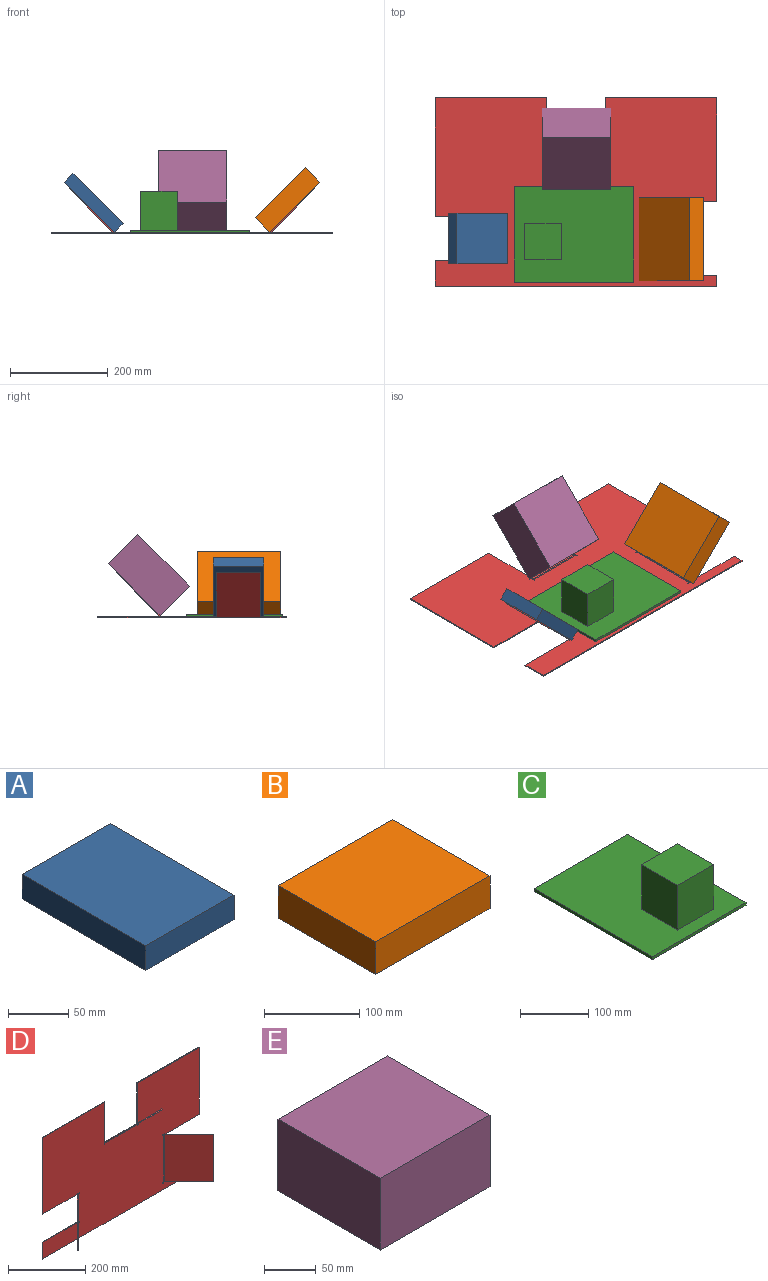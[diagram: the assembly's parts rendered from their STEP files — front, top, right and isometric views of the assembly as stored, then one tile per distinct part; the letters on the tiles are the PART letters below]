
ASSEMBLY  parts=5 mates=4
PART A: 6 faces, bbox 103x145x25 mm
  f0: plane 145x25mm, normal (-1,0,0), area 3625mm2, adj f1,f3,f4,f5
  f1: plane 103x25mm, normal (0,-1,0), area 2575mm2, adj f0,f2,f4,f5
  f2: plane 145x25mm, normal (1,0,0), area 3625mm2, adj f1,f3,f4,f5
  f3: plane 103x25mm, normal (0,1,0), area 2575mm2, adj f0,f2,f4,f5
  f4: plane 145x103mm, normal (0,0,1), area 14935mm2, adj f0,f1,f2,f3
  f5: plane 145x103mm, normal (0,0,-1), area 14935mm2, adj f0,f1,f2,f3
PART B: 6 faces, bbox 170x145x42 mm
  f0: plane 145x42mm, normal (-1,0,0), area 6090mm2, adj f1,f3,f4,f5
  f1: plane 170x42mm, normal (0,-1,0), area 7140mm2, adj f0,f2,f4,f5
  f2: plane 145x42mm, normal (1,0,0), area 6090mm2, adj f1,f3,f4,f5
  f3: plane 170x42mm, normal (0,1,0), area 7140mm2, adj f0,f2,f4,f5
  f4: plane 170x145mm, normal (0,0,1), area 24650mm2, adj f0,f1,f2,f3
  f5: plane 170x145mm, normal (0,0,-1), area 24650mm2, adj f0,f1,f2,f3
PART C: 11 faces, bbox 195x245x85 mm
  f0: plane 245x195mm, normal (0,0,1), area 42150mm2, adj f1,f2,f3,f4,f6,f7,f8,f9
  f1: plane 245x5mm, normal (-1,0,0), area 1225mm2, adj f0,f2,f4,f5
  f2: plane 195x5mm, normal (0,-1,0), area 975mm2, adj f0,f1,f3,f5
  f3: plane 245x5mm, normal (1,0,0), area 1225mm2, adj f0,f2,f4,f5
  f4: plane 195x5mm, normal (0,1,0), area 975mm2, adj f0,f1,f3,f5
  f5: plane 245x195mm, normal (0,0,-1), area 47775mm2, adj f1,f2,f3,f4
  f6: plane 80x75mm, normal (-1,0,0), area 6000mm2, adj f0,f7,f9,f10
  f7: plane 80x75mm, normal (0,-1,0), area 6000mm2, adj f0,f6,f8,f10
  f8: plane 80x75mm, normal (1,0,0), area 6000mm2, adj f0,f7,f9,f10
  f9: plane 80x75mm, normal (0,1,0), area 6000mm2, adj f0,f6,f8,f10
  f10: plane 75x75mm, normal (0,0,1), area 5625mm2, adj f6,f7,f8,f9
PART D: 66 faces, bbox 575x93.3x385 mm
  f0: plane 126.44x2mm, normal (0,0,1), area 252.9mm2, adj f3,f4,f5,f38
  f1: plane 126.44x2mm, normal (0,0,-1), area 252.9mm2, adj f3,f4,f9,f30
  f2: plane 126.44x2mm, normal (1,0,0), area 252.9mm2, adj f3,f4,f12,f22
  f3: plane 575x385mm, normal (0,-1,0), area 174134.5mm2, adj f0,f1,f2,f5,f6,f7,f8,f9
  f4: plane 575x385mm, normal (0,1,0), area 174134.5mm2, adj f0,f1,f2,f5,f6,f7,f8,f9
  f5: plane 52.5x2mm, normal (-1,0,0), area 105mm2, adj f0,f3,f4,f6
  f6: plane 575x2mm, normal (0,0,-1), area 1150mm2, adj f3,f4,f5,f7
  f7: plane 22.5x2mm, normal (1,0,0), area 45mm2, adj f3,f4,f6,f8
  f8: plane 126.44x2mm, normal (0,0,1), area 252.9mm2, adj f3,f4,f7,f34
  f9: plane 212.5x2mm, normal (1,0,0), area 425mm2, adj f1,f3,f4,f10
  f10: plane 227.5x2mm, normal (0,0,1), area 455mm2, adj f3,f4,f9,f11
  f11: plane 126.44x2mm, normal (-1,0,0), area 252.9mm2, adj f3,f4,f10,f26
  f12: plane 227.5x2mm, normal (0,0,1), area 455mm2, adj f2,f3,f4,f13
  f13: plane 242.5x2mm, normal (-1,0,0), area 485mm2, adj f3,f4,f12,f14
  f14: plane 126.44x2mm, normal (0,0,-1), area 252.9mm2, adj f3,f4,f13,f18
  f15: plane 2.3x2mm, normal (0,0,1), area 4.6mm2, adj f3,f4,f16,f54
  f16: cylinder r=1.06mm len=2.13mm, axis (0,1,0), area 6.7mm2, adj f3,f4,f15,f17
  f17: plane 6.81x2mm, normal (0,0,-1), area 13.6mm2, adj f3,f4,f16,f18
  f18: plane 2.13x2mm, normal (1,0,0), area 4.3mm2, adj f3,f4,f14,f17
  f19: plane 6.81x2mm, normal (1,0,0), area 13.6mm2, adj f3,f4,f20,f22
  f20: cylinder r=1.06mm len=2.13mm, axis (0,1,0), area 6.7mm2, adj f3,f4,f19,f21
  f21: plane 2.3x2mm, normal (-1,0,0), area 4.6mm2, adj f3,f4,f20,f62
  f22: plane 2.13x2mm, normal (0,0,-1), area 4.3mm2, adj f2,f3,f4,f19
  f23: plane 2.3x2mm, normal (1,0,0), area 4.6mm2, adj f3,f4,f24,f63
  f24: cylinder r=1.06mm len=2.13mm, axis (0,1,0), area 6.7mm2, adj f3,f4,f23,f25
  f25: plane 6.81x2mm, normal (-1,0,0), area 13.6mm2, adj f3,f4,f24,f26
  f26: plane 2.13x2mm, normal (0,0,-1), area 4.2mm2, adj f3,f4,f11,f25
  f27: plane 6.81x2mm, normal (0,0,-1), area 13.6mm2, adj f3,f4,f28,f30
  f28: cylinder r=1.06mm len=2.13mm, axis (0,1,0), area 6.7mm2, adj f3,f4,f27,f29
  f29: plane 2.3x2mm, normal (0,0,1), area 4.6mm2, adj f3,f4,f28,f44
  f30: plane 2.13x2mm, normal (-1,0,0), area 4.3mm2, adj f1,f3,f4,f27
  f31: plane 2.3x2mm, normal (0,0,-1), area 4.6mm2, adj f3,f4,f32,f45
  f32: cylinder r=1.06mm len=2.13mm, axis (0,1,0), area 6.7mm2, adj f3,f4,f31,f33
  f33: plane 6.81x2mm, normal (0,0,1), area 13.6mm2, adj f3,f4,f32,f34
  f34: plane 2.13x2mm, normal (-1,0,0), area 4.2mm2, adj f3,f4,f8,f33
  f35: plane 6.81x2mm, normal (0,0,1), area 13.6mm2, adj f3,f4,f36,f38
  f36: cylinder r=1.06mm len=2.13mm, axis (0,1,0), area 6.7mm2, adj f3,f4,f35,f37
  f37: plane 2.3x2mm, normal (0,0,-1), area 4.6mm2, adj f3,f4,f36,f53
  f38: plane 2.13x2mm, normal (1,0,0), area 4.2mm2, adj f0,f3,f4,f35
  f39: plane 150x1.41mm, normal (0.71,-0.71,0), area 300mm2, adj f40,f41,f42,f43
  f40: plane 92.08x92.08mm, normal (0,0,1), area 256.4mm2, adj f39,f42,f43,f44
  f41: plane 92.08x92.08mm, normal (0,0,-1), area 256.4mm2, adj f39,f42,f43,f45
  f42: plane 150x90.66mm, normal (-0.71,-0.71,0), area 19232.8mm2, adj f39,f40,f41,f47
  f43: plane 150x90.66mm, normal (0.71,0.71,0), area 19232.8mm2, adj f39,f40,f41,f46
  f44: plane 3.04x2.67mm, normal (0,0,1), area 5.2mm2, adj f29,f40,f46,f47
  f45: plane 3.04x2.67mm, normal (0,0,-1), area 5.2mm2, adj f31,f41,f46,f47
  f46: cylinder r=4.3mm len=150mm, axis (0,0,1), area 506.6mm2, adj f4,f43,f44,f45
  f47: cylinder r=2.3mm len=150mm, axis (0,0,1), area 271mm2, adj f3,f42,f44,f45
  f48: plane 90x1.41mm, normal (-0.71,-0.71,0), area 180mm2, adj f49,f50,f51,f52
  f49: plane 92.08x92.08mm, normal (0,0,-1), area 256.4mm2, adj f48,f51,f52,f53
  f50: plane 92.08x92.08mm, normal (0,0,1), area 256.4mm2, adj f48,f51,f52,f54
  f51: plane 90.66x90.66mm, normal (0.71,-0.71,0), area 11539.7mm2, adj f48,f49,f50,f56
  f52: plane 90.66x90.66mm, normal (-0.71,0.71,0), area 11539.7mm2, adj f48,f49,f50,f55
  f53: plane 3.04x2.67mm, normal (0,0,-1), area 5.2mm2, adj f37,f49,f55,f56
  f54: plane 3.04x2.67mm, normal (0,0,1), area 5.2mm2, adj f15,f50,f55,f56
  f55: cylinder r=4.3mm len=90mm, axis (0,0,-1), area 303.9mm2, adj f4,f52,f53,f54
  f56: cylinder r=2.3mm len=90mm, axis (0,0,-1), area 162.6mm2, adj f3,f51,f53,f54
  f57: plane 120x1.41mm, normal (0,-0.71,0.71), area 240mm2, adj f58,f59,f60,f61
  f58: plane 92.08x92.08mm, normal (-1,0,0), area 256.4mm2, adj f57,f60,f61,f62
  f59: plane 92.08x92.08mm, normal (1,0,0), area 256.4mm2, adj f57,f60,f61,f63
  f60: plane 120x90.66mm, normal (0,-0.71,-0.71), area 15386.3mm2, adj f57,f58,f59,f65
  f61: plane 120x90.66mm, normal (0,0.71,0.71), area 15386.3mm2, adj f57,f58,f59,f64
  f62: plane 3.04x2.67mm, normal (-1,0,0), area 5.2mm2, adj f21,f58,f64,f65
  f63: plane 3.04x2.67mm, normal (1,0,0), area 5.2mm2, adj f23,f59,f64,f65
  f64: cylinder r=4.3mm len=120mm, axis (-1,0,0), area 405.3mm2, adj f4,f61,f62,f63
  f65: cylinder r=2.3mm len=120mm, axis (-1,0,0), area 216.8mm2, adj f3,f60,f62,f63
PART E: 6 faces, bbox 150x140x85 mm
  f0: plane 140x85mm, normal (-1,0,0), area 11900mm2, adj f1,f3,f4,f5
  f1: plane 150x85mm, normal (0,-1,0), area 12750mm2, adj f0,f2,f4,f5
  f2: plane 140x85mm, normal (1,0,0), area 11900mm2, adj f1,f3,f4,f5
  f3: plane 150x85mm, normal (0,1,0), area 12750mm2, adj f0,f2,f4,f5
  f4: plane 150x140mm, normal (0,0,1), area 21000mm2, adj f0,f1,f2,f3
  f5: plane 150x140mm, normal (0,0,-1), area 21000mm2, adj f0,f1,f2,f3
PLACE A rot(axis=(-0.36,0.36,-0.86),98.4deg) t=(63.65,339.92,197.9)mm
PLACE B rot(axis=(0.36,-0.36,-0.86),98.4deg) t=(483.39,371.61,95.65)mm
PLACE C rot(axis=(0,0,-1),90deg) t=(198.05,394.21,94.41)mm
PLACE D rot(axis=(-1,0,0),90deg) t=(126.94,190.92,75.73)mm
PLACE E rot(axis=(0.36,-0.36,0.86),98.4deg) t=(395.92,448.78,97.27)mm
MATE planar B.f5 <-> D.f42  axis (0.71,0,-0.71) through (534.66,286.61,146.92)mm
MATE planar A.f5 <-> D.f51  axis (-0.71,0,-0.71) through (114.92,288.42,146.64)mm
MATE planar C.f5 <-> D.f3  axis (0,0,-1) through (320.55,199.21,94.41)mm
MATE planar E.f5 <-> D.f60  axis (0,0.71,-0.71) through (325.92,501.81,150.3)mm
